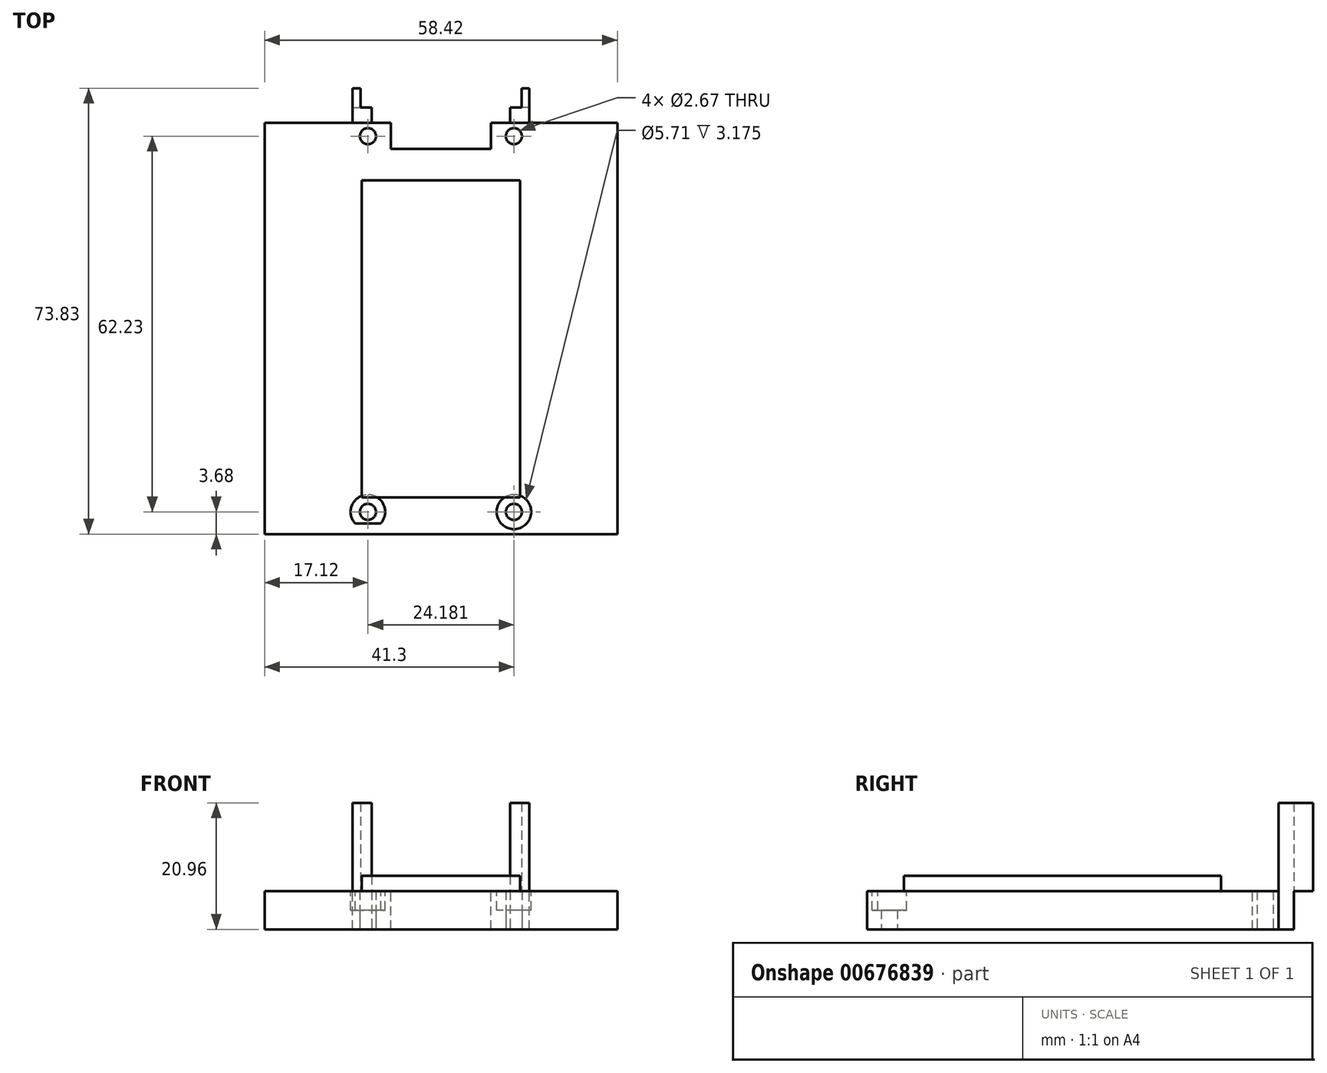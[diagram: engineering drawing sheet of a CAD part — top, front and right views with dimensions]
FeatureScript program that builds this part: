
annotation { "Feature Type Name" : "Feature", "Feature Type Description" : "" }
export const myFeature = defineFeature(function(context is Context, id is Id, definition is map)
    precondition{}
    {
        {
            var Q0;
            Q0=qCreatedBy(makeId("Top.planeOp"),FACE);
            var sketch = newSketch(context, id + "F0", { "sketchPlane" : qUnion([Q0])});
            skLineSegment(sketch, "E0.bottom", {"start": v(0, 0) * mm, "end": v(58.42, 0) * mm});
            skLineSegment(sketch, "E0.top", {"start": v(0, -66.34) * mm, "end": v(58.42, -66.34) * mm});
            skLineSegment(sketch, "E0.left", {"start": v(0, 0) * mm, "end": v(0, -66.34) * mm});
            skLineSegment(sketch, "E0.right", {"start": v(58.42, 0) * mm, "end": v(58.42, -66.34) * mm});
            skCircle(sketch, "E1", {"center": v(41.3, -64.44) * mm, "radius": 1.33 * mm});
            skCircle(sketch, "E2", {"center": v(17.12, -64.44) * mm, "radius": 1.33 * mm});
            skCircle(sketch, "E3", {"center": v(41.3, -2.2) * mm, "radius": 1.33 * mm});
            skCircle(sketch, "E4", {"center": v(17.12, -2.2) * mm, "radius": 1.33 * mm});
            skCircle(sketch, "E5", {"center": v(17.12, -64.44) * mm, "radius": 2.86 * mm});
            skCircle(sketch, "E6", {"center": v(41.3, -64.44) * mm, "radius": 2.86 * mm});
            skSolve(sketch);
        }
        {
            var Q0;
            Q0=makeQuery(id+"F0.imprint","IMPRINT",FACE,{"disambiguationData":[TD([[makeQuery(id+"F0.imprint","IMPRINT",EDGE,{"derivedFrom":sQuery(id+"F0.wireOp",EDGE,"E0.bottom")}),-1.0]])]});
            var Q1;
            Q1=makeQuery(id+"F0.imprint","IMPRINT",FACE,{"disambiguationData":[TD([[makeQuery(id+"F0.imprint","IMPRINT",EDGE,{"derivedFrom":sQuery(id+"F0.wireOp",EDGE,"E2")}),-1.0]])]});
            var Q2;
            Q2=makeQuery(id+"F0.imprint","IMPRINT",FACE,{"disambiguationData":[TD([[makeQuery(id+"F0.imprint","IMPRINT",EDGE,{"derivedFrom":sQuery(id+"F0.wireOp",EDGE,"E1")}),-1.0]])]});
            extrude(context, id + "F1", {"entities" : qUnion([Q0, Q1, Q2]), "depth" : 6.35 * mm, "offsetDistance" : 25.4 * mm});
        }
        {
            var Q0;
            Q0=makeQuery(id+"F1.opExtrude","CAP_FACE",FACE,{"disambiguationData":[OSD([sQuery(id+"F0.wireOp",EDGE,"E0.bottom"),sQuery(id+"F0.wireOp",EDGE,"E0.top"),sQuery(id+"F0.wireOp",EDGE,"E0.left"),sQuery(id+"F0.wireOp",EDGE,"E0.right"),sQuery(id+"F0.wireOp",EDGE,"E1"),sQuery(id+"F0.wireOp",EDGE,"E2"),sQuery(id+"F0.wireOp",EDGE,"E3"),sQuery(id+"F0.wireOp",EDGE,"E4")])],"isStart":false});
            var sketch = newSketch(context, id + "F2", { "sketchPlane" : qUnion([Q0])});
            skLineSegment(sketch, "E7.bottom", {"start": v(37.46, -4.32) * mm, "end": v(20.96, -4.32) * mm});
            skLineSegment(sketch, "E7.top", {"start": v(37.46, 0) * mm, "end": v(20.96, 0) * mm});
            skLineSegment(sketch, "E7.left", {"start": v(37.46, -4.32) * mm, "end": v(37.46, 0) * mm});
            skLineSegment(sketch, "E7.right", {"start": v(20.96, -4.32) * mm, "end": v(20.96, 0) * mm});
            skLineSegment(sketch, "E8.bottom", {"start": v(0, 0) * mm, "end": v(20.96, 0) * mm});
            skLineSegment(sketch, "E8.top", {"start": v(0, -4.32) * mm, "end": v(20.96, -4.32) * mm});
            skLineSegment(sketch, "E8.left", {"start": v(0, 0) * mm, "end": v(0, -4.32) * mm});
            skLineSegment(sketch, "E8.right", {"start": v(20.96, 0) * mm, "end": v(20.96, -4.32) * mm});
            skLineSegment(sketch, "E9.bottom", {"start": v(37.46, 0) * mm, "end": v(58.42, 0) * mm});
            skLineSegment(sketch, "E9.top", {"start": v(37.46, -4.32) * mm, "end": v(58.42, -4.32) * mm});
            skLineSegment(sketch, "E9.left", {"start": v(37.46, 0) * mm, "end": v(37.46, -4.32) * mm});
            skLineSegment(sketch, "E9.right", {"start": v(58.42, 0) * mm, "end": v(58.42, -4.32) * mm});
            skLineSegment(sketch, "E10.bottom", {"start": v(20.96, 0) * mm, "end": v(13.3, 0) * mm});
            skLineSegment(sketch, "E10.top", {"start": v(20.96, -4.32) * mm, "end": v(13.3, -4.32) * mm});
            skLineSegment(sketch, "E10.right", {"start": v(13.3, 0) * mm, "end": v(13.3, -4.32) * mm});
            skLineSegment(sketch, "E11.bottom", {"start": v(37.46, 0) * mm, "end": v(45.12, 0) * mm});
            skLineSegment(sketch, "E11.top", {"start": v(37.46, -4.32) * mm, "end": v(45.12, -4.32) * mm});
            skLineSegment(sketch, "E11.right", {"start": v(45.12, 0) * mm, "end": v(45.12, -4.32) * mm});
            skLineSegment(sketch, "E12.bottom", {"start": v(20.96, 0) * mm, "end": v(19.56, 0) * mm});
            skLineSegment(sketch, "E12.top", {"start": v(20.96, -4.32) * mm, "end": v(19.56, -4.32) * mm});
            skLineSegment(sketch, "E12.right", {"start": v(19.56, 0) * mm, "end": v(19.56, -4.32) * mm});
            skLineSegment(sketch, "E13.bottom", {"start": v(37.46, 0) * mm, "end": v(38.86, 0) * mm});
            skLineSegment(sketch, "E13.top", {"start": v(37.46, -4.32) * mm, "end": v(38.86, -4.32) * mm});
            skLineSegment(sketch, "E13.right", {"start": v(38.86, 0) * mm, "end": v(38.86, -4.32) * mm});
            skSolve(sketch);
        }
        {
            var Q0;
            Q0=makeQuery(id+"F2.imprint","IMPRINT",FACE,{"disambiguationData":[TD([[makeQuery(id+"F2.imprint","IMPRINT",EDGE,{"derivedFrom":sQuery(id+"F2.wireOp",EDGE,"E7.bottom")}),-1.0]])]});
            extrude(context, id + "F3", {"entities" : qUnion([Q0]), "operationType" : NewBodyOperationType.REMOVE, "endBound" : BoundingType.THROUGH_ALL, "oppositeDirection" : true, "depth" : 25.4 * mm, "offsetDistance" : 25.4 * mm});
        }
        {
            var Q0;
            Q0=makeQuery(id+"F1.opExtrude","CAP_FACE",FACE,{"disambiguationData":[OSD([sQuery(id+"F0.wireOp",EDGE,"E0.bottom"),sQuery(id+"F0.wireOp",EDGE,"E0.top"),sQuery(id+"F0.wireOp",EDGE,"E0.left"),sQuery(id+"F0.wireOp",EDGE,"E0.right"),sQuery(id+"F0.wireOp",EDGE,"E1"),sQuery(id+"F0.wireOp",EDGE,"E2"),sQuery(id+"F0.wireOp",EDGE,"E3"),sQuery(id+"F0.wireOp",EDGE,"E4")])],"isStart":false});
            var sketch = newSketch(context, id + "F4", { "sketchPlane" : qUnion([Q0])});
            skLineSegment(sketch, "E14.bottom", {"start": v(16.13, -4.32) * mm, "end": v(42.3, -4.32) * mm});
            skLineSegment(sketch, "E14.top", {"start": v(16.13, -62.03) * mm, "end": v(42.3, -62.03) * mm});
            skLineSegment(sketch, "E14.left", {"start": v(16.13, -4.32) * mm, "end": v(16.13, -62.03) * mm});
            skLineSegment(sketch, "E14.right", {"start": v(42.3, -4.32) * mm, "end": v(42.3, -62.03) * mm});
            skLineSegment(sketch, "E15.bottom", {"start": v(16.13, -4.32) * mm, "end": v(21.34, -4.32) * mm});
            skLineSegment(sketch, "E15.top", {"start": v(16.13, -62.03) * mm, "end": v(21.34, -62.03) * mm});
            skLineSegment(sketch, "E15.right", {"start": v(21.34, -4.32) * mm, "end": v(21.34, -62.03) * mm});
            skLineSegment(sketch, "E16.top", {"start": v(16.13, -9.52) * mm, "end": v(42.3, -9.52) * mm});
            skLineSegment(sketch, "E16.left", {"start": v(16.13, -4.32) * mm, "end": v(16.13, -9.52) * mm});
            skLineSegment(sketch, "E16.right", {"start": v(42.3, -4.32) * mm, "end": v(42.3, -9.52) * mm});
            skLineSegment(sketch, "E17.bottom", {"start": v(42.3, -4.32) * mm, "end": v(37.08, -4.32) * mm});
            skLineSegment(sketch, "E17.top", {"start": v(42.3, -62.03) * mm, "end": v(37.08, -62.03) * mm});
            skLineSegment(sketch, "E17.right", {"start": v(37.08, -4.32) * mm, "end": v(37.08, -62.03) * mm});
            skSolve(sketch);
        }
        {
            var Q0;
            Q0=makeQuery(id+"F1.opExtrude","SWEPT_FACE",FACE,{"disambiguationData":[OSD([sQuery(id+"F0.wireOp",EDGE,"E0.top")])]});
            extrude(context, id + "F5", {"entities" : qUnion([Q0]), "operationType" : NewBodyOperationType.ADD, "depth" : 1.78 * mm, "offsetDistance" : 25.4 * mm});
        }
        {
            var Q0;
            Q0=makeQuery(id+"F0.imprint","IMPRINT",FACE,{"disambiguationData":[TD([[makeQuery(id+"F0.imprint","IMPRINT",EDGE,{"derivedFrom":sQuery(id+"F0.wireOp",EDGE,"E1")}),-1.0]])]});
            var Q1;
            Q1=makeQuery(id+"F0.imprint","IMPRINT",FACE,{"disambiguationData":[TD([[makeQuery(id+"F0.imprint","IMPRINT",EDGE,{"derivedFrom":sQuery(id+"F0.wireOp",EDGE,"E2")}),-1.0]])]});
            var Q2;
            {var subQ0=sQuery(id+"F0.wireOp",EDGE,"E5");var subQ1=sQuery(id+"F0.wireOp",EDGE,"E0.top");var subQ2=makeQuery(id+"F0.imprint","INTERSECT",VERTEX,{"disambiguationData":[OD(0.0)],"derivedFrom":[subQ1,subQ0]});Q2=makeQuery(id+"F0.imprint","IMPRINT",FACE,{"disambiguationData":[TD([[makeQuery(id+"F0.imprint","IMPRINT",EDGE,{"disambiguationData":[TD([[subQ2,-1.0]])],"derivedFrom":subQ1}),-1.0]])]});}
            var Q3;
            {var subQ0=sQuery(id+"F0.wireOp",EDGE,"E6");var subQ1=sQuery(id+"F0.wireOp",EDGE,"E0.top");var subQ2=makeQuery(id+"F0.imprint","INTERSECT",VERTEX,{"disambiguationData":[OD(0.0)],"derivedFrom":[subQ1,subQ0]});Q3=makeQuery(id+"F0.imprint","IMPRINT",FACE,{"disambiguationData":[TD([[makeQuery(id+"F0.imprint","IMPRINT",EDGE,{"disambiguationData":[TD([[subQ2,-1.0]])],"derivedFrom":subQ1}),-1.0]])]});}
            extrude(context, id + "F6", {"entities" : qUnion([Q0, Q1, Q2, Q3]), "operationType" : NewBodyOperationType.ADD, "depth" : 6.6 * mm, "offsetDistance" : 25.4 * mm});
        }
        {
            var Q0;
            Q0=makeQuery(id+"F6.opExtrude","CAP_FACE",FACE,{"disambiguationData":[OSD([sQuery(id+"F0.wireOp",EDGE,"E2"),sQuery(id+"F0.wireOp",EDGE,"E5")])],"isStart":false});
            var Q1;
            Q1=makeQuery(id+"F6.opExtrude","CAP_FACE",FACE,{"disambiguationData":[OSD([sQuery(id+"F0.wireOp",EDGE,"E1"),sQuery(id+"F0.wireOp",EDGE,"E6")])],"isStart":false});
            extrude(context, id + "F7", {"entities" : qUnion([Q0, Q1]), "operationType" : NewBodyOperationType.REMOVE, "oppositeDirection" : true, "depth" : 3.43 * mm, "offsetDistance" : 25.4 * mm});
        }
        {
            var Q0;
            {var subQ0=sQuery(id+"F4.wireOp",EDGE,"E14.top");Q0=makeQuery(id+"F4.imprint","IMPRINT",FACE,{"disambiguationData":[TD([[makeQuery(id+"F4.imprint","IMPRINT",EDGE,{"derivedFrom":subQ0}),1.0]])]});}
            extrude(context, id + "F8", {"entities" : qUnion([Q0]), "operationType" : NewBodyOperationType.ADD, "depth" : 2.54 * mm, "offsetDistance" : 25.4 * mm});
        }
        {
            var Q0;
            {var subQ5=sQuery(id+"F0.wireOp",EDGE,"E0.left");var subQ7=sQuery(id+"F0.wireOp",EDGE,"E0.bottom");Q0=makeQuery(id+"F3.boolean.opBoolean","SPLIT",FACE,{"disambiguationData":[TD([makeQuery(id+"F1.opExtrude","SWEPT_FACE",FACE,{"disambiguationData":[OSD([subQ5])]})])],"derivedFrom":makeQuery(id+"F1.opExtrude","SWEPT_FACE",FACE,{"disambiguationData":[OSD([subQ7])]})});}
            var sketch = newSketch(context, id + "F9", { "sketchPlane" : qUnion([Q0])});
            skLineSegment(sketch, "E18.bottom", {"start": v(-20.96, 0) * mm, "end": v(-14.6, 0) * mm});
            skLineSegment(sketch, "E18.top", {"start": v(-20.96, 6.35) * mm, "end": v(-14.6, 6.35) * mm});
            skLineSegment(sketch, "E18.left", {"start": v(-20.96, 0) * mm, "end": v(-20.96, 6.35) * mm});
            skLineSegment(sketch, "E18.right", {"start": v(-14.6, 0) * mm, "end": v(-14.6, 6.35) * mm});
            skSolve(sketch);
        }
        {
            var Q0;
            {var subQ4=sQuery(id+"F0.wireOp",EDGE,"E0.right");var subQ7=sQuery(id+"F0.wireOp",EDGE,"E0.bottom");Q0=makeQuery(id+"F3.boolean.opBoolean","SPLIT",FACE,{"disambiguationData":[TD([makeQuery(id+"F1.opExtrude","SWEPT_FACE",FACE,{"disambiguationData":[OSD([subQ4])]})])],"derivedFrom":makeQuery(id+"F1.opExtrude","SWEPT_FACE",FACE,{"disambiguationData":[OSD([subQ7])]})});}
            var sketch = newSketch(context, id + "F10", { "sketchPlane" : qUnion([Q0])});
            skLineSegment(sketch, "E19.bottom", {"start": v(-37.46, 0) * mm, "end": v(-43.81, 0) * mm});
            skLineSegment(sketch, "E19.top", {"start": v(-37.46, 6.35) * mm, "end": v(-43.81, 6.35) * mm});
            skLineSegment(sketch, "E19.left", {"start": v(-37.46, 0) * mm, "end": v(-37.46, 6.35) * mm});
            skLineSegment(sketch, "E19.right", {"start": v(-43.81, 0) * mm, "end": v(-43.81, 6.35) * mm});
            skSolve(sketch);
        }
        {
            var Q0;
            Q0=makeQuery(id+"F9.imprint","IMPRINT",FACE,{"disambiguationData":[TD([[makeQuery(id+"F9.imprint","IMPRINT",EDGE,{"derivedFrom":sQuery(id+"F9.wireOp",EDGE,"E18.bottom")}),-1.0]])]});
            var Q1;
            Q1=makeQuery(id+"F10.imprint","IMPRINT",FACE,{"disambiguationData":[TD([[makeQuery(id+"F10.imprint","IMPRINT",EDGE,{"derivedFrom":sQuery(id+"F10.wireOp",EDGE,"E19.bottom")}),-1.0]])]});
            extrude(context, id + "F11", {"entities" : qUnion([Q0, Q1]), "operationType" : NewBodyOperationType.ADD, "depth" : 2.54 * mm, "offsetDistance" : 25.4 * mm});
        }
        {
            var Q0;
            {var subQ0=sQuery(id+"F0.wireOp",EDGE,"E0.top");Q0=makeQuery(id+"F11.boolean.opBoolean","MERGE",FACE,{"derivedFrom":[makeQuery(id+"F5.boolean.opBoolean","MERGE",FACE,{"derivedFrom":[makeQuery(id+"F1.opExtrude","CAP_FACE",FACE,{"disambiguationData":[OSD([sQuery(id+"F0.wireOp",EDGE,"E0.bottom"),subQ0,sQuery(id+"F0.wireOp",EDGE,"E0.left"),sQuery(id+"F0.wireOp",EDGE,"E0.right"),sQuery(id+"F0.wireOp",EDGE,"E1"),sQuery(id+"F0.wireOp",EDGE,"E2"),sQuery(id+"F0.wireOp",EDGE,"E3"),sQuery(id+"F0.wireOp",EDGE,"E4")])],"isStart":false}),makeQuery(id+"F5.opExtrude","SWEPT_FACE",FACE,{"disambiguationData":[OSD([subQ0]),TDD([makeQuery(id+"F1.opExtrude","CAP_EDGE",EDGE,{"disambiguationData":[OSD([subQ0])],"isStart":false})])]})]}),makeQuery(id+"F11.opExtrude","SWEPT_FACE",FACE,{"disambiguationData":[OSD([sQuery(id+"F9.wireOp",EDGE,"E18.top")])]}),makeQuery(id+"F11.opExtrude","SWEPT_FACE",FACE,{"disambiguationData":[OSD([sQuery(id+"F10.wireOp",EDGE,"E19.top")])]})]});}
            var sketch = newSketch(context, id + "F12", { "sketchPlane" : qUnion([Q0])});
            skLineSegment(sketch, "E20.bottom", {"start": v(14.6, 2.54) * mm, "end": v(20.96, 2.54) * mm});
            skLineSegment(sketch, "E20.top", {"start": v(14.6, 0) * mm, "end": v(20.96, 0) * mm});
            skLineSegment(sketch, "E20.left", {"start": v(14.6, 2.54) * mm, "end": v(14.6, 0) * mm});
            skLineSegment(sketch, "E20.right", {"start": v(20.96, 2.54) * mm, "end": v(20.96, 0) * mm});
            skLineSegment(sketch, "E21.bottom", {"start": v(37.46, 2.54) * mm, "end": v(43.81, 2.54) * mm});
            skLineSegment(sketch, "E21.top", {"start": v(37.46, 0) * mm, "end": v(43.81, 0) * mm});
            skLineSegment(sketch, "E21.left", {"start": v(37.46, 2.54) * mm, "end": v(37.46, 0) * mm});
            skLineSegment(sketch, "E21.right", {"start": v(43.81, 2.54) * mm, "end": v(43.81, 0) * mm});
            skSolve(sketch);
        }
        {
            var Q0;
            Q0 = qSketchRegion(id + "F12", true);
            extrude(context, id + "F13", {"entities" : qUnion([Q0]), "operationType" : NewBodyOperationType.ADD, "depth" : 14.6 * mm, "offsetDistance" : 25.4 * mm});
        }
        {
            var Q0;
            {var subQ0=sQuery(id+"F0.wireOp",EDGE,"E0.top");Q0=makeQuery(id+"F11.boolean.opBoolean","MERGE",FACE,{"derivedFrom":[makeQuery(id+"F5.boolean.opBoolean","MERGE",FACE,{"derivedFrom":[makeQuery(id+"F1.opExtrude","CAP_FACE",FACE,{"disambiguationData":[OSD([sQuery(id+"F0.wireOp",EDGE,"E0.bottom"),subQ0,sQuery(id+"F0.wireOp",EDGE,"E0.left"),sQuery(id+"F0.wireOp",EDGE,"E0.right"),sQuery(id+"F0.wireOp",EDGE,"E1"),sQuery(id+"F0.wireOp",EDGE,"E2"),sQuery(id+"F0.wireOp",EDGE,"E3"),sQuery(id+"F0.wireOp",EDGE,"E4")])],"isStart":true}),makeQuery(id+"F5.opExtrude","SWEPT_FACE",FACE,{"disambiguationData":[OSD([subQ0]),TDD([makeQuery(id+"F1.opExtrude","CAP_EDGE",EDGE,{"disambiguationData":[OSD([subQ0])],"isStart":true})])]})]}),makeQuery(id+"F11.opExtrude","SWEPT_FACE",FACE,{"disambiguationData":[OSD([sQuery(id+"F9.wireOp",EDGE,"E18.bottom")])]}),makeQuery(id+"F11.opExtrude","SWEPT_FACE",FACE,{"disambiguationData":[OSD([sQuery(id+"F10.wireOp",EDGE,"E19.bottom")])]})]});}
            var sketch = newSketch(context, id + "F14", { "sketchPlane" : qUnion([Q0])});
            skLineSegment(sketch, "E22.bottom", {"start": v(20.96, -2.54) * mm, "end": v(17.78, -2.54) * mm});
            skLineSegment(sketch, "E22.top", {"start": v(20.96, 0) * mm, "end": v(17.78, 0) * mm});
            skLineSegment(sketch, "E22.left", {"start": v(20.96, -2.54) * mm, "end": v(20.96, 0) * mm});
            skLineSegment(sketch, "E22.right", {"start": v(17.78, -2.54) * mm, "end": v(17.78, 0) * mm});
            skLineSegment(sketch, "E23.bottom", {"start": v(37.46, -2.54) * mm, "end": v(40.64, -2.54) * mm});
            skLineSegment(sketch, "E23.top", {"start": v(37.46, 0) * mm, "end": v(40.64, 0) * mm});
            skLineSegment(sketch, "E23.left", {"start": v(37.46, -2.54) * mm, "end": v(37.46, 0) * mm});
            skLineSegment(sketch, "E23.right", {"start": v(40.64, -2.54) * mm, "end": v(40.64, 0) * mm});
            skSolve(sketch);
        }
        {
            var Q0;
            Q0=makeQuery(id+"F14.imprint","IMPRINT",FACE,{"disambiguationData":[TD([[makeQuery(id+"F14.imprint","IMPRINT",EDGE,{"derivedFrom":sQuery(id+"F14.wireOp",EDGE,"E22.bottom")}),1.0]])]});
            var Q1;
            Q1=makeQuery(id+"F14.imprint","IMPRINT",FACE,{"disambiguationData":[TD([[makeQuery(id+"F14.imprint","IMPRINT",EDGE,{"derivedFrom":sQuery(id+"F14.wireOp",EDGE,"E23.bottom")}),1.0]])]});
            extrude(context, id + "F15", {"entities" : qUnion([Q0, Q1]), "operationType" : NewBodyOperationType.REMOVE, "endBound" : BoundingType.THROUGH_ALL, "oppositeDirection" : true, "depth" : 25.4 * mm, "offsetDistance" : 25.4 * mm});
        }
        {
            var Q0;
            Q0=makeQuery(id+"F13.boolean.opBoolean","MERGE",FACE,{"derivedFrom":[makeQuery(id+"F11.opExtrude","CAP_FACE",FACE,{"disambiguationData":[OSD([sQuery(id+"F10.wireOp",EDGE,"E19.bottom"),sQuery(id+"F10.wireOp",EDGE,"E19.top"),sQuery(id+"F10.wireOp",EDGE,"E19.left"),sQuery(id+"F10.wireOp",EDGE,"E19.right")])],"isStart":false}),makeQuery(id+"F13.opExtrude","SWEPT_FACE",FACE,{"disambiguationData":[OSD([sQuery(id+"F12.wireOp",EDGE,"E21.bottom")])]})]});
            var sketch = newSketch(context, id + "F16", { "sketchPlane" : qUnion([Q0])});
            skLineSegment(sketch, "E24.bottom", {"start": v(-43.81, 20.96) * mm, "end": v(-42.54, 20.96) * mm});
            skLineSegment(sketch, "E24.top", {"start": v(-43.81, 6.35) * mm, "end": v(-42.54, 6.35) * mm});
            skLineSegment(sketch, "E24.left", {"start": v(-43.81, 20.96) * mm, "end": v(-43.81, 6.35) * mm});
            skLineSegment(sketch, "E24.right", {"start": v(-42.54, 20.96) * mm, "end": v(-42.54, 6.35) * mm});
            skSolve(sketch);
        }
        {
            var Q0;
            Q0=makeQuery(id+"F13.boolean.opBoolean","MERGE",FACE,{"derivedFrom":[makeQuery(id+"F11.opExtrude","CAP_FACE",FACE,{"disambiguationData":[OSD([sQuery(id+"F9.wireOp",EDGE,"E18.bottom"),sQuery(id+"F9.wireOp",EDGE,"E18.top"),sQuery(id+"F9.wireOp",EDGE,"E18.left"),sQuery(id+"F9.wireOp",EDGE,"E18.right")])],"isStart":false}),makeQuery(id+"F13.opExtrude","SWEPT_FACE",FACE,{"disambiguationData":[OSD([sQuery(id+"F12.wireOp",EDGE,"E20.bottom")])]})]});
            var sketch = newSketch(context, id + "F17", { "sketchPlane" : qUnion([Q0])});
            skLineSegment(sketch, "E25.bottom", {"start": v(-14.6, 20.96) * mm, "end": v(-15.88, 20.96) * mm});
            skLineSegment(sketch, "E25.top", {"start": v(-14.6, 6.35) * mm, "end": v(-15.87, 6.35) * mm});
            skLineSegment(sketch, "E25.left", {"start": v(-14.6, 20.96) * mm, "end": v(-14.6, 6.35) * mm});
            skLineSegment(sketch, "E25.right", {"start": v(-15.88, 20.96) * mm, "end": v(-15.88, 6.35) * mm});
            skSolve(sketch);
        }
        {
            var Q0;
            Q0=makeQuery(id+"F16.imprint","IMPRINT",FACE,{"disambiguationData":[TD([[makeQuery(id+"F16.imprint","IMPRINT",EDGE,{"derivedFrom":sQuery(id+"F16.wireOp",EDGE,"E24.bottom")}),1.0]])]});
            var Q1;
            Q1=makeQuery(id+"F17.imprint","IMPRINT",FACE,{"disambiguationData":[TD([[makeQuery(id+"F17.imprint","IMPRINT",EDGE,{"derivedFrom":sQuery(id+"F17.wireOp",EDGE,"E25.bottom")}),1.0]])]});
            extrude(context, id + "F18", {"entities" : qUnion([Q0, Q1]), "operationType" : NewBodyOperationType.ADD, "depth" : 3.17 * mm, "offsetDistance" : 25.4 * mm});
        }
    });
